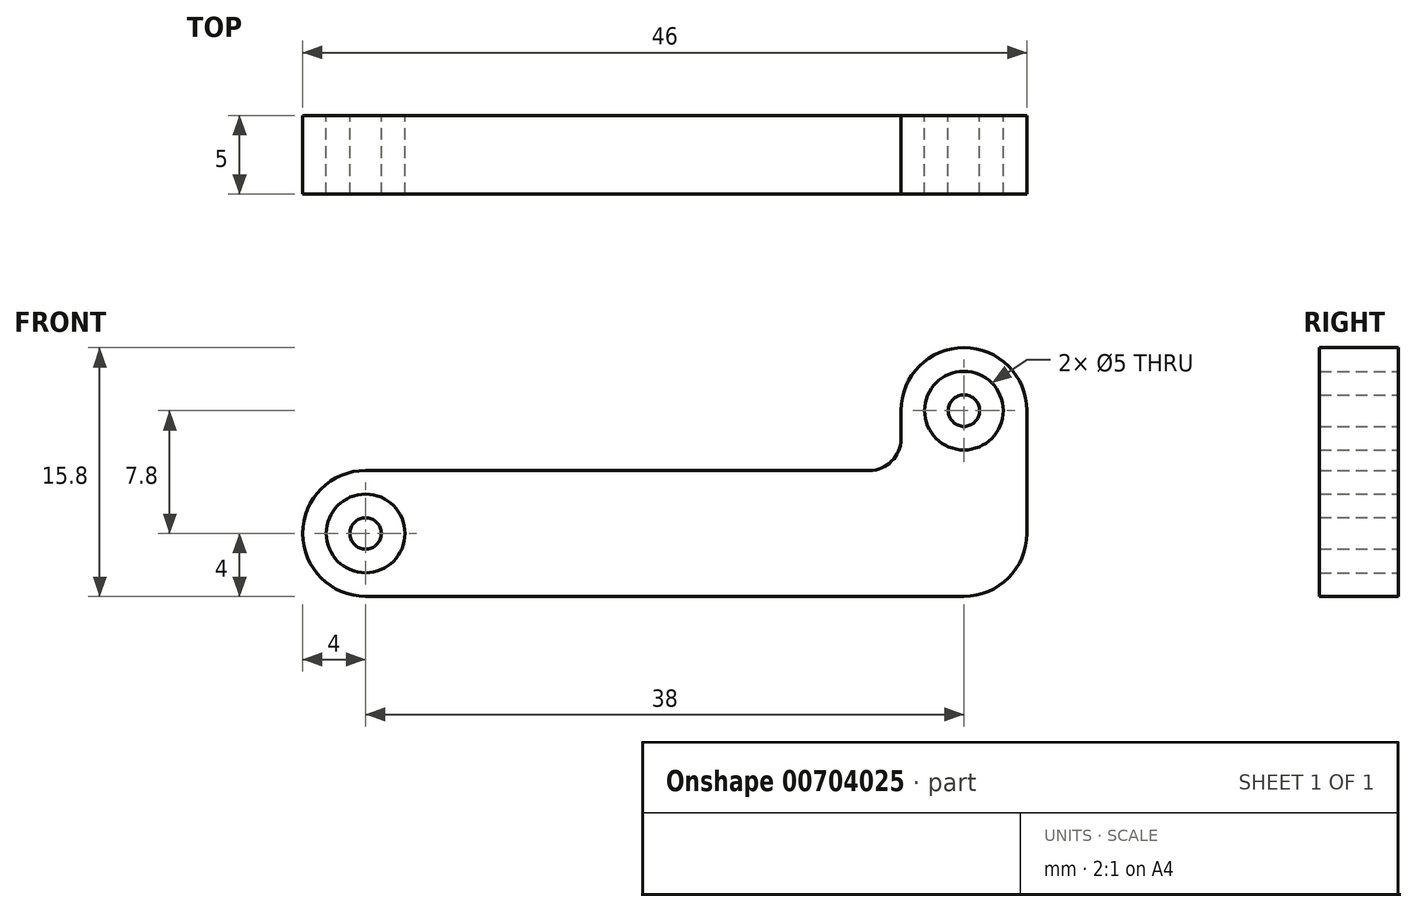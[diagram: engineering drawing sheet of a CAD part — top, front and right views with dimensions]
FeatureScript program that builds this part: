
annotation { "Feature Type Name" : "Feature", "Feature Type Description" : "" }
export const myFeature = defineFeature(function(context is Context, id is Id, definition is map)
    precondition{}
    {
        {
            var Q0;
            Q0=qCreatedBy(makeId("Front.planeOp"),FACE);
            var sketch = newSketch(context, id + "F0", { "sketchPlane" : qUnion([Q0])});
            skArc(sketch, "E0", {"start": v(0, 4) * mm, "mid": v(-4, 0) * mm, "end": v(0, -4) * mm});
            skCircle(sketch, "E1", {"center": v(0, 0) * mm, "radius": 2.5 * mm});
            skCircle(sketch, "E2", {"center": v(0, 0) * mm, "radius": 1 * mm});
            skArc(sketch, "E3", {"start": v(42, 7.8) * mm, "mid": v(38, 11.8) * mm, "end": v(34, 7.8) * mm});
            skCircle(sketch, "E4", {"center": v(38, 7.8) * mm, "radius": 2.5 * mm});
            skCircle(sketch, "E5", {"center": v(38, 7.8) * mm, "radius": 1 * mm});
            skLineSegment(sketch, "E6", {"start": v(0, 4) * mm, "end": v(32, 4) * mm});
            skLineSegment(sketch, "E7.0", {"start": v(0, -4) * mm, "end": v(38, -4) * mm});
            skLineSegment(sketch, "E8", {"start": v(34, 7.8) * mm, "end": v(34, 6) * mm});
            skLineSegment(sketch, "E9.0", {"start": v(42, 7.8) * mm, "end": v(42, 0) * mm});
            skPoint(sketch, "E10.visualSharp", {"position": v(34, 4) * mm});
            skArc(sketch, "E10.filletArc", {"start": v(32, 4) * mm, "mid": v(33.41, 4.59) * mm, "end": v(34, 6) * mm});
            skPoint(sketch, "E11.visualSharp", {"position": v(42, -4) * mm});
            skArc(sketch, "E11.filletArc", {"start": v(38, -4) * mm, "mid": v(40.83, -2.83) * mm, "end": v(42, 0) * mm});
            skSolve(sketch);
        }
        {
            var Q0;
            Q0=makeQuery(id+"F0.imprint","IMPRINT",FACE,{"disambiguationData":[TD([[makeQuery(id+"F0.imprint","IMPRINT",EDGE,{"derivedFrom":sQuery(id+"F0.wireOp",EDGE,"E0")}),1.0]])]});
            var Q1;
            Q1=makeQuery(id+"F0.imprint","IMPRINT",FACE,{"disambiguationData":[TD([[makeQuery(id+"F0.imprint","IMPRINT",EDGE,{"derivedFrom":sQuery(id+"F0.wireOp",EDGE,"E2")}),1.0]])]});
            var Q2;
            Q2=makeQuery(id+"F0.imprint","IMPRINT",FACE,{"disambiguationData":[TD([[makeQuery(id+"F0.imprint","IMPRINT",EDGE,{"derivedFrom":sQuery(id+"F0.wireOp",EDGE,"E5")}),1.0]])]});
            extrude(context, id + "F1", {"entities" : qUnion([Q0, Q1, Q2]), "depth" : 5 * mm, "offsetDistance" : 25 * mm});
        }
    });
